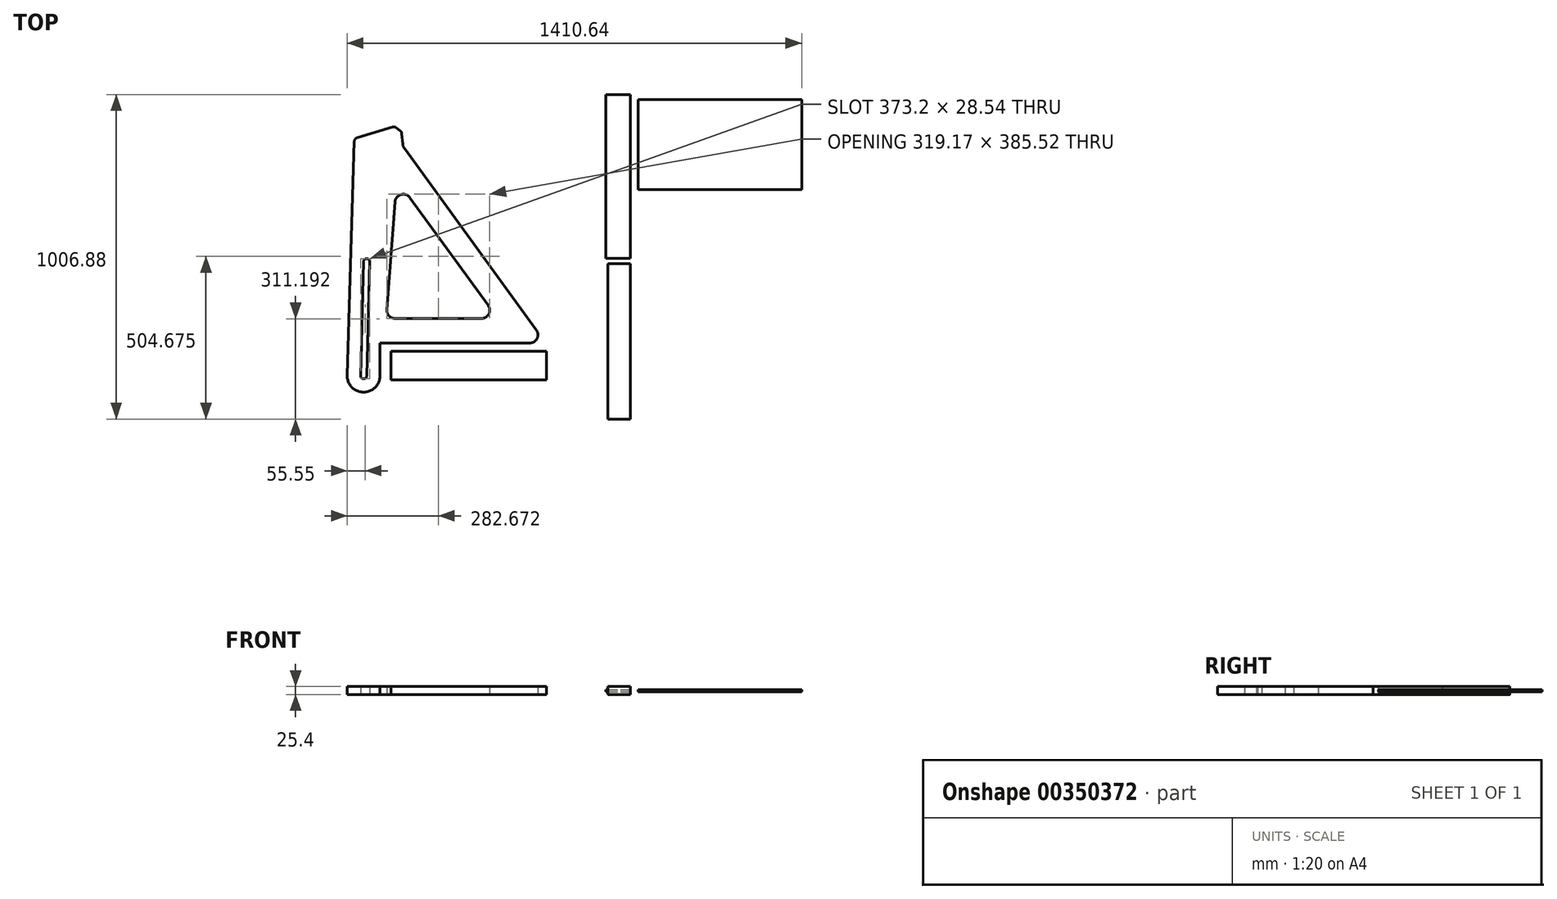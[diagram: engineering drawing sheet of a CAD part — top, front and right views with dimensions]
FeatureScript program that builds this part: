
annotation { "Feature Type Name" : "Feature", "Feature Type Description" : "" }
export const myFeature = defineFeature(function(context is Context, id is Id, definition is map)
    precondition{}
    {
        {
            var Q0;
            Q0=qCreatedBy(makeId("Top.planeOp"),FACE);
            var sketch = newSketch(context, id + "F0", { "sketchPlane" : qUnion([Q0])});
            skLineSegment(sketch, "E0.bottom", {"start": v(-118.27, 322.88) * mm, "end": v(389.73, 322.88) * mm});
            skLineSegment(sketch, "E0.top", {"start": v(-118.27, 602.28) * mm, "end": v(389.73, 602.28) * mm});
            skLineSegment(sketch, "E0.left", {"start": v(-118.27, 322.88) * mm, "end": v(-118.27, 602.28) * mm});
            skLineSegment(sketch, "E0.right", {"start": v(389.73, 322.88) * mm, "end": v(389.73, 602.28) * mm});
            skLineSegment(sketch, "E1.bottom", {"start": v(-218.4, 109.91) * mm, "end": v(-142.2, 109.91) * mm});
            skLineSegment(sketch, "E1.top", {"start": v(-218.4, 617.91) * mm, "end": v(-142.2, 617.91) * mm});
            skLineSegment(sketch, "E1.left", {"start": v(-218.4, 109.91) * mm, "end": v(-218.4, 617.91) * mm});
            skLineSegment(sketch, "E1.right", {"start": v(-142.2, 109.91) * mm, "end": v(-142.2, 617.91) * mm});
            skLineSegment(sketch, "E2.bottom", {"start": v(-212.05, -388.97) * mm, "end": v(-142.2, -388.97) * mm});
            skLineSegment(sketch, "E2.top", {"start": v(-212.05, 93.63) * mm, "end": v(-142.2, 93.63) * mm});
            skLineSegment(sketch, "E2.left", {"start": v(-212.05, -388.97) * mm, "end": v(-212.05, 93.63) * mm});
            skLineSegment(sketch, "E2.right", {"start": v(-142.2, -388.97) * mm, "end": v(-142.2, 93.63) * mm});
            skLineSegment(sketch, "E3.bottom", {"start": v(-884.54, -267.86) * mm, "end": v(-401.94, -267.86) * mm});
            skLineSegment(sketch, "E3.top", {"start": v(-884.54, -178.96) * mm, "end": v(-401.94, -178.96) * mm});
            skLineSegment(sketch, "E3.left", {"start": v(-884.54, -267.86) * mm, "end": v(-884.54, -178.96) * mm});
            skLineSegment(sketch, "E3.right", {"start": v(-401.94, -267.86) * mm, "end": v(-401.94, -178.96) * mm});
            skLineSegment(sketch, "E4", {"start": v(-919.3, -254.86) * mm, "end": v(-919.3, -153.26) * mm});
            skLineSegment(sketch, "E5", {"start": v(-919.3, -153.26) * mm, "end": v(-454.42, -153.26) * mm});
            skLineSegment(sketch, "E6", {"start": v(-433.87, -112.93) * mm, "end": v(-843.76, 451.23) * mm});
            skLineSegment(sketch, "E7", {"start": v(-998.86, 472.4) * mm, "end": v(-1020.82, -251.78) * mm});
            skArc(sketch, "E8", {"start": v(-1020.82, -251.78) * mm, "mid": v(-971.65, -305.63) * mm, "end": v(-919.3, -254.86) * mm});
            skArc(sketch, "E9", {"start": v(-454.42, -153.26) * mm, "mid": v(-431.8, -139.39) * mm, "end": v(-433.87, -112.93) * mm});
            skLineSegment(sketch, "E10", {"start": v(-989.82, 484.18) * mm, "end": v(-880.37, 517.14) * mm});
            skLineSegment(sketch, "E11", {"start": v(-848.48, 463.62) * mm, "end": v(-851.85, 497.14) * mm});
            skLineSegment(sketch, "E12", {"start": v(-856.9, 506.06) * mm, "end": v(-869.12, 515.16) * mm});
            skPoint(sketch, "E13.visualSharp", {"position": v(-998.58, 481.54) * mm});
            skArc(sketch, "E13.filletArc", {"start": v(-989.82, 484.18) * mm, "mid": v(-996.24, 479.74) * mm, "end": v(-998.86, 472.4) * mm});
            skPoint(sketch, "E14.visualSharp", {"position": v(-874.24, 518.98) * mm});
            skArc(sketch, "E14.filletArc", {"start": v(-869.12, 515.16) * mm, "mid": v(-874.5, 517.48) * mm, "end": v(-880.37, 517.14) * mm});
            skPoint(sketch, "E15.visualSharp", {"position": v(-852.4, 502.71) * mm});
            skArc(sketch, "E15.filletArc", {"start": v(-851.85, 497.14) * mm, "mid": v(-853.43, 502.13) * mm, "end": v(-856.9, 506.06) * mm});
            skPoint(sketch, "E16.visualSharp", {"position": v(-847.8, 456.79) * mm});
            skArc(sketch, "E16.filletArc", {"start": v(-848.48, 463.62) * mm, "mid": v(-846.94, 457.11) * mm, "end": v(-843.76, 451.23) * mm});
            skLineSegment(sketch, "E17.left", {"start": v(-960.59, -255.11) * mm, "end": v(-951.09, 99.04) * mm});
            skLineSegment(sketch, "E17.right", {"start": v(-979.63, -254.6) * mm, "end": v(-970.13, 99.55) * mm});
            skArc(sketch, "E18", {"start": v(-951.09, 99.04) * mm, "mid": v(-960.36, 108.82) * mm, "end": v(-970.13, 99.55) * mm});
            skArc(sketch, "E19", {"start": v(-979.63, -254.6) * mm, "mid": v(-970.24, -264.38) * mm, "end": v(-960.58, -254.86) * mm});
            skArc(sketch, "E20", {"start": v(-897.82, -49.74) * mm, "mid": v(-891.12, -68.92) * mm, "end": v(-872.5, -77.06) * mm});
            skArc(sketch, "E21", {"start": v(-826.62, 298) * mm, "mid": v(-854.1, 307.51) * mm, "end": v(-872.5, 285) * mm});
            skArc(sketch, "E22", {"start": v(-603.97, -77.06) * mm, "mid": v(-581.34, -63.19) * mm, "end": v(-583.42, -36.73) * mm});
            skLineSegment(sketch, "E23", {"start": v(-872.5, -77.06) * mm, "end": v(-603.97, -77.06) * mm});
            skLineSegment(sketch, "E24", {"start": v(-583.42, -36.73) * mm, "end": v(-826.62, 298) * mm});
            skLineSegment(sketch, "E25", {"start": v(-872.5, 285) * mm, "end": v(-897.82, -49.74) * mm});
            skLineSegment(sketch, "E26.trimOffspring", {"start": v(-960.58, -254.86) * mm, "end": v(-960.58, -254.86) * mm});
            skPoint(sketch, "E27.orphan", {"position": v(-1020.9, -254.86) * mm});
            skSolve(sketch);
        }
        {
            var Q0;
            Q0=makeQuery(id+"F0.imprint","IMPRINT",FACE,{"disambiguationData":[TD([[makeQuery(id+"F0.imprint","IMPRINT",EDGE,{"derivedFrom":sQuery(id+"F0.wireOp",EDGE,"E3.bottom")}),1.0]])]});
            var Q1;
            Q1=makeQuery(id+"F0.imprint","IMPRINT",FACE,{"disambiguationData":[TD([[makeQuery(id+"F0.imprint","IMPRINT",EDGE,{"derivedFrom":sQuery(id+"F0.wireOp",EDGE,"E4")}),1.0]])]});
            var Q2;
            Q2=makeQuery(id+"F0.imprint","IMPRINT",FACE,{"disambiguationData":[TD([[makeQuery(id+"F0.imprint","IMPRINT",EDGE,{"derivedFrom":sQuery(id+"F0.wireOp",EDGE,"E2.bottom")}),1.0]])]});
            extrude(context, id + "F1", {"entities" : qUnion([Q0, Q1, Q2]), "endBound" : BoundingType.SYMMETRIC, "depth" : 25.4 * mm});
        }
        {
            var Q0;
            Q0=makeQuery(id+"F0.imprint","IMPRINT",FACE,{"disambiguationData":[TD([[makeQuery(id+"F0.imprint","IMPRINT",EDGE,{"derivedFrom":sQuery(id+"F0.wireOp",EDGE,"E1.bottom")}),1.0]])]});
            var Q1;
            Q1=makeQuery(id+"F0.imprint","IMPRINT",FACE,{"disambiguationData":[TD([[makeQuery(id+"F0.imprint","IMPRINT",EDGE,{"derivedFrom":sQuery(id+"F0.wireOp",EDGE,"E0.bottom")}),1.0]])]});
            extrude(context, id + "F2", {"entities" : qUnion([Q0, Q1]), "endBound" : BoundingType.SYMMETRIC, "depth" : 6.35 * mm});
        }
    });
